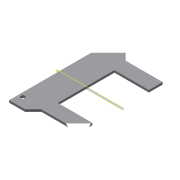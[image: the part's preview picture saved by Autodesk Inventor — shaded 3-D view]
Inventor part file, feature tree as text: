
AUTODESK INVENTOR PART (.ipt)
format: ipt  version: 2014 (Build 180170000, 170)  size: 108,032 bytes
history: native  units: mm
features: reference x12, extrude x2, sketch x2, plane x1, mirror x1
ambient origin geometry x8: Origin, YZ Plane, XZ Plane, XY Plane, X Axis, Y Axis, Z Axis, Center Point
bodies: Volumenkörper1 (feature_tree)
feature tree (18):
  extrude  "Extrusion1"  TaperAngle=135.0deg  [1 undecoded]
  extrude  "Extrusion2"  Depth=5.0mm
  plane  "Arbeitsebene1"
  mirror  "Spiegeln1"
  sketch  "Skizze1"  dims[d0=1.6mm d1=0.0mm d2=135.0deg]
  reference  "Referenz1"
  reference  "Referenz2"
  reference  "Referenz3"
  reference  "Referenz4"
  reference  "Referenz5"
  reference  "Referenz6"
  reference  "Referenz7"
  reference  "Referenz8"
  reference  "Referenz9"
  reference  "Referenz10"
  reference  "Referenz11"
  reference  "Referenz12"
  sketch  "Skizze2"  dims[d3=1.6mm d4=0.0mm d5=7.0mm d6=7.0mm d7=5.0mm]
note: 1 required parameter value undecoded (feature->parameter linkage not recoverable at this tier; creation-order binding heuristic only, values carry confidence <= 0.55)
